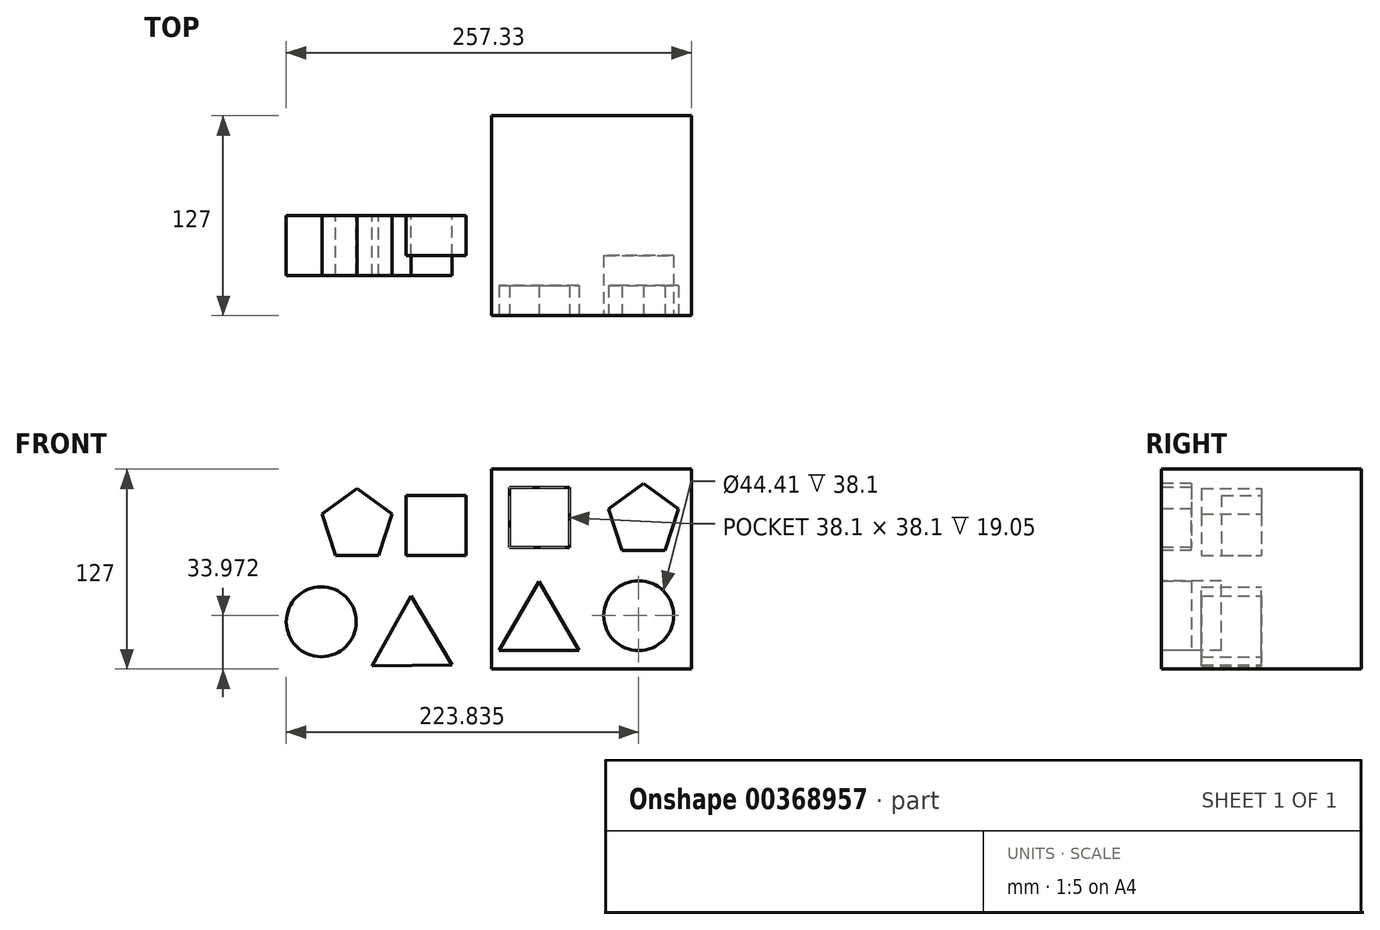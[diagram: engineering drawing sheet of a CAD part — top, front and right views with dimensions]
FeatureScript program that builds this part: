
annotation { "Feature Type Name" : "Feature", "Feature Type Description" : "" }
export const myFeature = defineFeature(function(context is Context, id is Id, definition is map)
    precondition{}
    {
        {
            var Q0;
            Q0=qCreatedBy(makeId("Front.planeOp"),FACE);
            var sketch = newSketch(context, id + "F0", { "sketchPlane" : qUnion([Q0])});
            skLineSegment(sketch, "E0.bottom", {"start": v(63.5, 63.5) * mm, "end": v(-63.5, 63.5) * mm});
            skLineSegment(sketch, "E0.top", {"start": v(63.5, -63.5) * mm, "end": v(-63.5, -63.5) * mm});
            skLineSegment(sketch, "E0.left", {"start": v(63.5, 63.5) * mm, "end": v(63.5, -63.5) * mm});
            skLineSegment(sketch, "E0.right", {"start": v(-63.5, 63.5) * mm, "end": v(-63.5, -63.5) * mm});
            skPoint(sketch, "E0.middle", {"position": v(0, 0) * mm});
            skSolve(sketch);
        }
        {
            var Q0;
            Q0 = qSketchRegion(id + "F0", true);
            extrude(context, id + "F1", {"entities" : qUnion([Q0]), "endBound" : BoundingType.SYMMETRIC, "depth" : 127 * mm});
        }
        {
            var Q0;
            Q0=makeQuery(id+"F1.opExtrude","CAP_FACE",FACE,{"disambiguationData":[OSD([sQuery(id+"F0.wireOp",EDGE,"E0.bottom"),sQuery(id+"F0.wireOp",EDGE,"E0.top"),sQuery(id+"F0.wireOp",EDGE,"E0.left"),sQuery(id+"F0.wireOp",EDGE,"E0.right")])],"isStart":false});
            var sketch = newSketch(context, id + "F2", { "sketchPlane" : qUnion([Q0])});
            skLineSegment(sketch, "E1.bottom", {"start": v(-52.09, 51.82) * mm, "end": v(-13.99, 51.82) * mm});
            skLineSegment(sketch, "E1.top", {"start": v(-52.09, 13.72) * mm, "end": v(-13.99, 13.72) * mm});
            skLineSegment(sketch, "E1.left", {"start": v(-52.09, 51.82) * mm, "end": v(-52.09, 13.72) * mm});
            skLineSegment(sketch, "E1.right", {"start": v(-13.99, 51.82) * mm, "end": v(-13.99, 13.72) * mm});
            skPoint(sketch, "E1.middle", {"position": v(-33.04, 32.77) * mm});
            skSolve(sketch);
        }
        {
            var Q0;
            Q0 = qSketchRegion(id + "F2", true);
            extrude(context, id + "F3", {"entities" : qUnion([Q0]), "operationType" : NewBodyOperationType.REMOVE, "endBound" : BoundingType.SYMMETRIC, "oppositeDirection" : true, "depth" : 38.1 * mm});
        }
        {
            var Q0;
            Q0=makeQuery(id+"F1.opExtrude","CAP_FACE",FACE,{"disambiguationData":[OSD([sQuery(id+"F0.wireOp",EDGE,"E0.bottom"),sQuery(id+"F0.wireOp",EDGE,"E0.top"),sQuery(id+"F0.wireOp",EDGE,"E0.left"),sQuery(id+"F0.wireOp",EDGE,"E0.right")])],"isStart":false});
            var sketch = newSketch(context, id + "F4", { "sketchPlane" : qUnion([Q0])});
            skCircle(sketch, "E2.cCircle", {"center": v(33.05, 30.84) * mm, "radius": 19 * mm, "construction": true});
            skLineSegment(sketch, "E2.0", {"start": v(33.05, 54.32) * mm, "end": v(55.39, 38.1) * mm});
            skLineSegment(sketch, "E2.1", {"start": v(55.39, 38.1) * mm, "end": v(46.86, 11.85) * mm});
            skLineSegment(sketch, "E2.2", {"start": v(46.86, 11.85) * mm, "end": v(19.25, 11.85) * mm});
            skLineSegment(sketch, "E2.3", {"start": v(19.25, 11.85) * mm, "end": v(10.72, 38.1) * mm});
            skLineSegment(sketch, "E2.4", {"start": v(10.72, 38.1) * mm, "end": v(33.05, 54.32) * mm});
            skPoint(sketch, "E2.0.midPoint", {"position": v(44.22, 46.2) * mm});
            skSolve(sketch);
        }
        {
            var Q0;
            Q0 = qSketchRegion(id + "F4", true);
            extrude(context, id + "F5", {"entities" : qUnion([Q0]), "operationType" : NewBodyOperationType.REMOVE, "endBound" : BoundingType.SYMMETRIC, "oppositeDirection" : true, "depth" : 38.1 * mm});
        }
        {
            var Q0;
            Q0=makeQuery(id+"F1.opExtrude","CAP_FACE",FACE,{"disambiguationData":[OSD([sQuery(id+"F0.wireOp",EDGE,"E0.bottom"),sQuery(id+"F0.wireOp",EDGE,"E0.top"),sQuery(id+"F0.wireOp",EDGE,"E0.left"),sQuery(id+"F0.wireOp",EDGE,"E0.right")])],"isStart":false});
            var sketch = newSketch(context, id + "F6", { "sketchPlane" : qUnion([Q0])});
            skCircle(sketch, "E3.cCircle", {"center": v(-33.3, -36.97) * mm, "radius": 14.66 * mm, "construction": true});
            skLineSegment(sketch, "E3.0", {"start": v(-7.9, -51.64) * mm, "end": v(-58.7, -51.64) * mm});
            skLineSegment(sketch, "E3.1", {"start": v(-58.7, -51.64) * mm, "end": v(-33.3, -7.65) * mm});
            skLineSegment(sketch, "E3.2", {"start": v(-33.3, -7.65) * mm, "end": v(-7.9, -51.64) * mm});
            skPoint(sketch, "E3.0.midPoint", {"position": v(-33.3, -51.64) * mm});
            skSolve(sketch);
        }
        {
            var Q0;
            Q0 = qSketchRegion(id + "F6", true);
            extrude(context, id + "F7", {"entities" : qUnion([Q0]), "operationType" : NewBodyOperationType.REMOVE, "endBound" : BoundingType.SYMMETRIC, "oppositeDirection" : true, "depth" : 38.1 * mm});
        }
        {
            var Q0;
            Q0=makeQuery(id+"F1.opExtrude","CAP_FACE",FACE,{"disambiguationData":[OSD([sQuery(id+"F0.wireOp",EDGE,"E0.bottom"),sQuery(id+"F0.wireOp",EDGE,"E0.top"),sQuery(id+"F0.wireOp",EDGE,"E0.left"),sQuery(id+"F0.wireOp",EDGE,"E0.right")])],"isStart":false});
            var sketch = newSketch(context, id + "F8", { "sketchPlane" : qUnion([Q0])});
            skCircle(sketch, "E4", {"center": v(30, -29.53) * mm, "radius": 22.2 * mm});
            skSolve(sketch);
        }
        {
            var Q0;
            Q0 = qSketchRegion(id + "F8", true);
            extrude(context, id + "F9", {"entities" : qUnion([Q0]), "operationType" : NewBodyOperationType.REMOVE, "oppositeDirection" : true, "depth" : 38.1 * mm});
        }
        {
            var Q0;
            Q0=qCreatedBy(makeId("Front.planeOp"),FACE);
            var sketch = newSketch(context, id + "F10", { "sketchPlane" : qUnion([Q0])});
            skLineSegment(sketch, "E5.bottom", {"start": v(-117.8, 46.97) * mm, "end": v(-79.7, 46.97) * mm});
            skLineSegment(sketch, "E5.top", {"start": v(-117.8, 8.87) * mm, "end": v(-79.7, 8.87) * mm});
            skLineSegment(sketch, "E5.left", {"start": v(-117.8, 46.97) * mm, "end": v(-117.8, 8.87) * mm});
            skLineSegment(sketch, "E5.right", {"start": v(-79.7, 46.97) * mm, "end": v(-79.7, 8.87) * mm});
            skSolve(sketch);
        }
        {
            var Q0;
            Q0=makeQuery(id+"F10.imprint","IMPRINT",FACE,{"disambiguationData":[TD([[makeQuery(id+"F10.imprint","IMPRINT",EDGE,{"derivedFrom":sQuery(id+"F10.wireOp",EDGE,"E5.bottom")}),-1.0]])]});
            extrude(context, id + "F11", {"entities" : qUnion([Q0]), "depth" : 25.4 * mm});
        }
        {
            var Q0;
            Q0=qCreatedBy(makeId("Front.planeOp"),FACE);
            var sketch = newSketch(context, id + "F12", { "sketchPlane" : qUnion([Q0])});
            skCircle(sketch, "E6.cCircle", {"center": v(-114.02, -46.44) * mm, "radius": 14.66 * mm, "construction": true});
            skLineSegment(sketch, "E6.0", {"start": v(-114.43, -17.11) * mm, "end": v(-88.41, -60.75) * mm});
            skLineSegment(sketch, "E6.1", {"start": v(-88.41, -60.75) * mm, "end": v(-139.2, -61.46) * mm});
            skLineSegment(sketch, "E6.2", {"start": v(-139.2, -61.46) * mm, "end": v(-114.43, -17.11) * mm});
            skPoint(sketch, "E6.0.midPoint", {"position": v(-105.8, -33.1) * mm});
            skSolve(sketch);
        }
        {
            var Q0;
            Q0=makeQuery(id+"F12.imprint","IMPRINT",FACE,{"disambiguationData":[TD([[makeQuery(id+"F12.imprint","IMPRINT",EDGE,{"derivedFrom":sQuery(id+"F12.wireOp",EDGE,"E6.0")}),-1.0]])]});
            extrude(context, id + "F13", {"entities" : qUnion([Q0]), "depth" : 38.1 * mm});
        }
        {
            var Q0;
            Q0=qCreatedBy(makeId("Front.planeOp"),FACE);
            var sketch = newSketch(context, id + "F14", { "sketchPlane" : qUnion([Q0])});
            skCircle(sketch, "E7.cCircle", {"center": v(-148.87, 27.68) * mm, "radius": 19 * mm, "construction": true});
            skLineSegment(sketch, "E7.0", {"start": v(-126.54, 34.94) * mm, "end": v(-135.07, 8.68) * mm});
            skLineSegment(sketch, "E7.1", {"start": v(-135.07, 8.68) * mm, "end": v(-162.67, 8.68) * mm});
            skLineSegment(sketch, "E7.2", {"start": v(-162.67, 8.68) * mm, "end": v(-171.2, 34.94) * mm});
            skLineSegment(sketch, "E7.3", {"start": v(-171.2, 34.94) * mm, "end": v(-148.87, 51.16) * mm});
            skLineSegment(sketch, "E7.4", {"start": v(-148.87, 51.16) * mm, "end": v(-126.54, 34.94) * mm});
            skPoint(sketch, "E7.0.midPoint", {"position": v(-122.68, 21.81) * mm});
            skSolve(sketch);
        }
        {
            var Q0;
            Q0 = qSketchRegion(id + "F14", true);
            extrude(context, id + "F15", {"entities" : qUnion([Q0]), "depth" : 38.1 * mm});
        }
        {
            var Q0;
            Q0=qCreatedBy(makeId("Front.planeOp"),FACE);
            var sketch = newSketch(context, id + "F16", { "sketchPlane" : qUnion([Q0])});
            skCircle(sketch, "E8", {"center": v(-171.62, -33.42) * mm, "radius": 22.2 * mm});
            skSolve(sketch);
        }
        {
            var Q0;
            Q0 = qSketchRegion(id + "F16", true);
            extrude(context, id + "F17", {"entities" : qUnion([Q0]), "depth" : 38.1 * mm});
        }
    });
